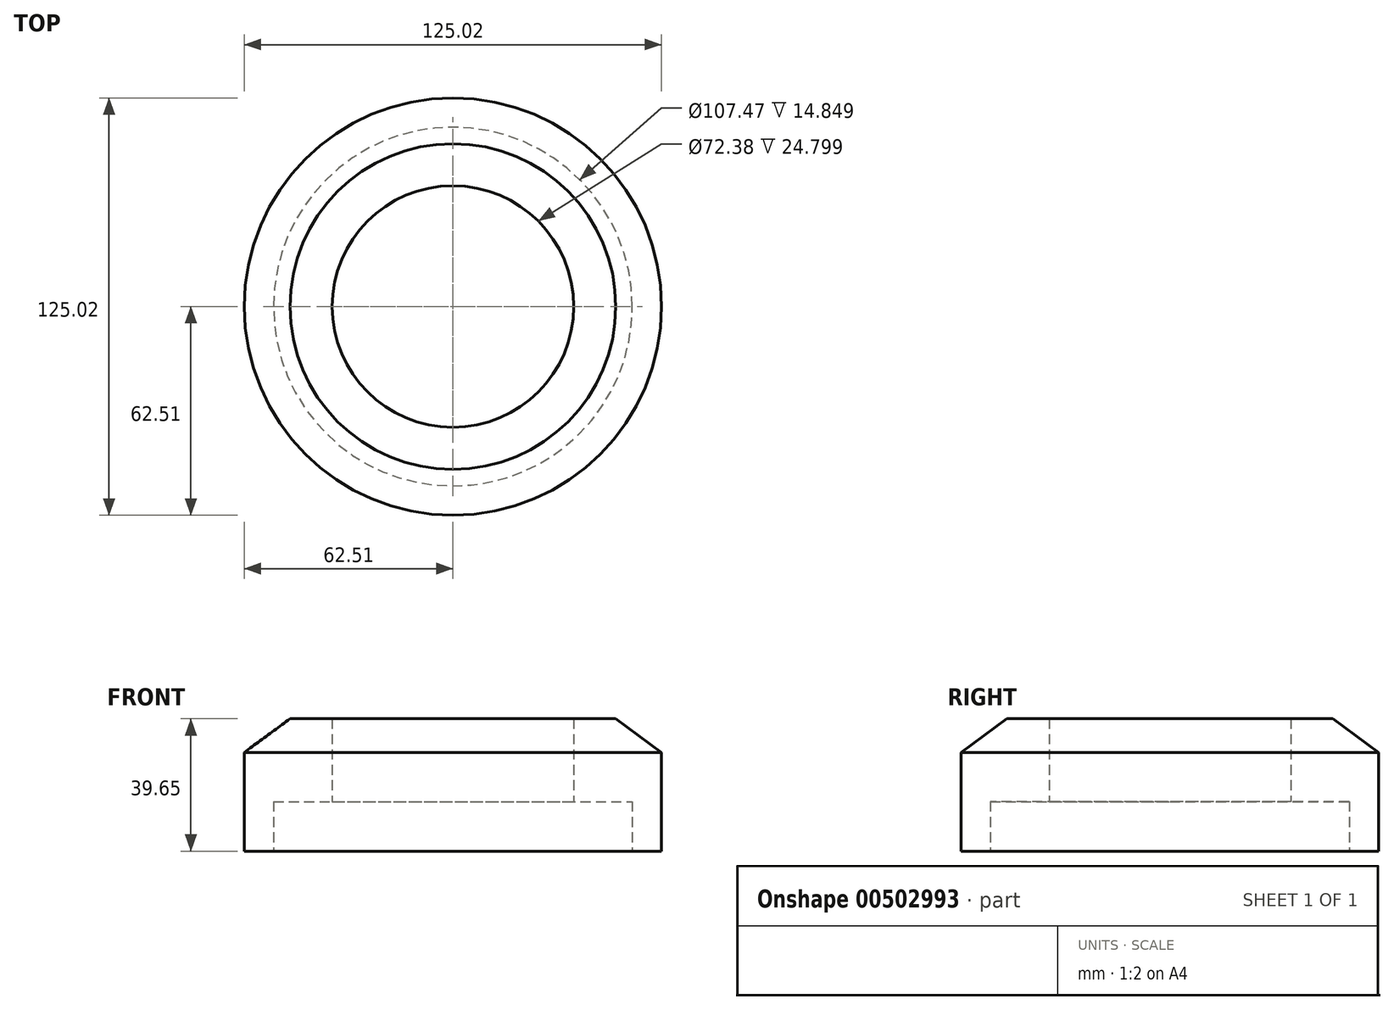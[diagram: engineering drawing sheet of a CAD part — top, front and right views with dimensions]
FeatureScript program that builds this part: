
annotation { "Feature Type Name" : "Feature", "Feature Type Description" : "" }
export const myFeature = defineFeature(function(context is Context, id is Id, definition is map)
    precondition{}
    {
        {
            var Q0;
            Q0=qCreatedBy(makeId("Front.planeOp"),FACE);
            var sketch = newSketch(context, id + "F0", { "sketchPlane" : qUnion([Q0])});
            skLineSegment(sketch, "E0", {"start": v(0, -34.86) * mm, "end": v(0, 65.96) * mm});
            skSolve(sketch);
        }
        {
            var Q0;
            Q0=qCreatedBy(makeId("Front.planeOp"),FACE);
            var sketch = newSketch(context, id + "F1", { "sketchPlane" : qUnion([Q0])});
            skLineSegment(sketch, "E1", {"start": v(-62.5, 0) * mm, "end": v(-62.5, 29.59) * mm});
            skLineSegment(sketch, "E2", {"start": v(-62.5, 29.59) * mm, "end": v(-48.8, 39.65) * mm});
            skLineSegment(sketch, "E3", {"start": v(-48.8, 39.65) * mm, "end": v(-36.19, 39.65) * mm});
            skLineSegment(sketch, "E4", {"start": v(-36.19, 39.65) * mm, "end": v(-36.19, 14.85) * mm});
            skLineSegment(sketch, "E5", {"start": v(-36.19, 14.85) * mm, "end": v(-53.74, 14.85) * mm});
            skLineSegment(sketch, "E6", {"start": v(-53.74, 14.85) * mm, "end": v(-53.74, 0) * mm});
            skLineSegment(sketch, "E7", {"start": v(-53.74, 0) * mm, "end": v(-62.5, 0) * mm});
            skSolve(sketch);
        }
        {
            var Q0;
            Q0=makeQuery(id+"F1.imprint","IMPRINT",FACE,{"disambiguationData":[TD([[makeQuery(id+"F1.imprint","IMPRINT",EDGE,{"derivedFrom":sQuery(id+"F1.wireOp",EDGE,"E1")}),-1.0]])]});
            var Q1;
            Q1=sQuery(id+"F0.wireOp",EDGE,"E0");
            revolve(context, id + "F2", {"entities" : qUnion([Q0]), "axis" : qUnion([Q1]), "revolveType" : RevolveType.FULL});
        }
    });
